# Revit family: Pop_Up_Drain-Push-American_Standard-Universal-8888XXX_Series
name_source: partatom
category: Plumbing Fixtures
units: mm (PartAtom-declared; Revit-internal decimal feet)

## family parameters
Always vertical = No
Cut with Voids When Loaded = No
OmniClass Number = 23.45.55.21
OmniClass Title = Drains (Wastes)
Part Type = Normal
Room Calculation Point = No
Round Connector Dimension = Use Diameter
Shared = Yes
Work Plane-Based = Yes

## types (8) — shared parameters
ADA Compliant = Yes
Assembly Code = D2040100
CW Connection = No
CWFU = 1.5
Default Elevation = 0"
Diameter = 2 1/2"
HW Connection = No
HWFU = 1.5
Height = 8 1/2"
IAPMO Compliance = These products meet or exceed:ASME A112.18.1, CSA B125.2
Installation Type = Lavatory Sink Inside
Manufacturer = American Standard
Product Documentation Link = https://lixil.cdn.celum.cloud
Product Page URL = https://www.americanstandard.ca
URL = https://www.americanstandard.ca
Vent Connection = No
WFU = 2
Waste Connection = Yes
Waste Connection Diameter = 1 1/4"

## per-type parameters (varying)
| type | Description | Finish | Material | Void Extrusion Distance |
| 8888095.002 | Push Pop-up Drain With Overflow | Brass-American Standard-002-Polished Chrome | Brass-American Standard-002-Polished Chrome | 1/2" |
| 8888095.013 | Push Pop-up Drain With Overflow | Brass-American Standard-013-Polished Nickel | Brass-American Standard-013-Polished Nickel | 1/2" |
| 8888095.278 | Push Pop-up Drain With Overflow | Brass-American Standard-278-Legacy Bronze | Brass-American Standard-278-Legacy Bronze | 1/2" |
| 8888095.295 | Push Pop-up Drain With Overflow | Brass-American Standard-295-Brushed Nickel | Brass-American Standard-295-Brushed Nickel | 1/2" |
| 8888112.002 | Push Pop-up Drain Without Overflow | Brass-American Standard-002-Polished Chrome | Brass-American Standard-002-Polished Chrome | 1" |
| 8888112.295 | Push Pop-up Drain Without Overflow | Brass-American Standard-295-Brushed Nickel | Brass-American Standard-295-Brushed Nickel | 1" |
| 8888112.013 | Push Pop-up Drain Without Overflow | Brass-American Standard-013-Polished Nickel | Brass-American Standard-013-Polished Nickel | 1" |
| 8888112.278 | Push Pop-up Drain Without Overflow | Brass-American Standard-278-Legacy Bronze | Brass-American Standard-278-Legacy Bronze | 1" |

note: column(s) folded — value = type name in every type: Model

## geometry (parser evidence)
native form markers: Sweep x2
no freeform markers — native parametric forms only
